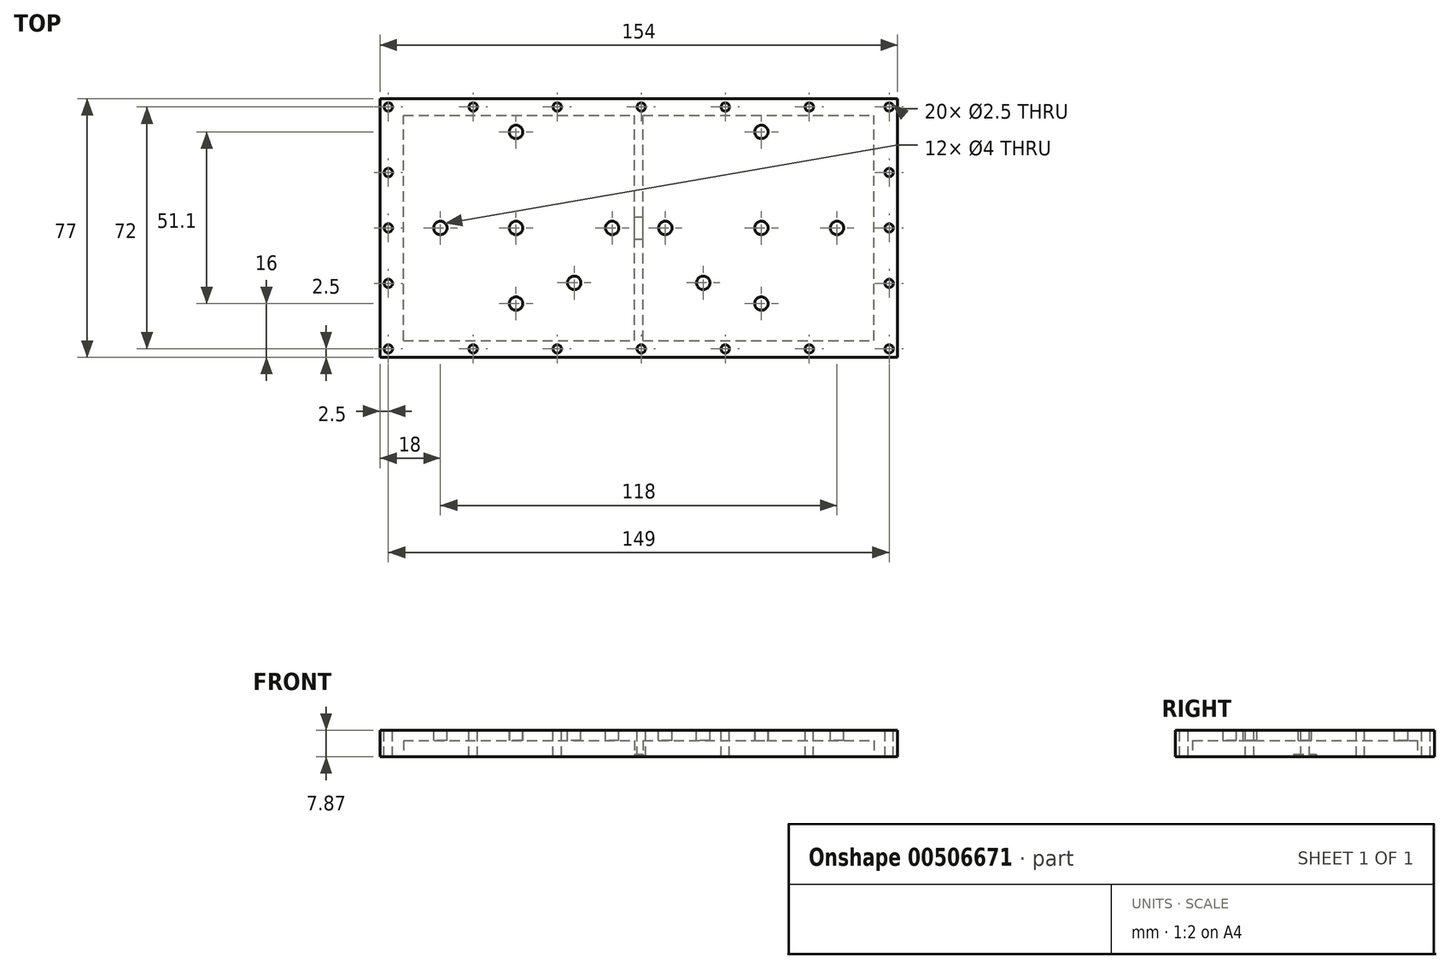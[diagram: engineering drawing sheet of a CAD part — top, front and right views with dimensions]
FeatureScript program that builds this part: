
annotation { "Feature Type Name" : "Feature", "Feature Type Description" : "" }
export const myFeature = defineFeature(function(context is Context, id is Id, definition is map)
    precondition{}
    {
        {
            var Q0;
            Q0=qCreatedBy(makeId("Top.planeOp"),FACE);
            var sketch = newSketch(context, id + "F0", { "sketchPlane" : qUnion([Q0])});
            skLineSegment(sketch, "E0.bottom", {"start": v(0, 0) * mm, "end": v(154, 0) * mm});
            skLineSegment(sketch, "E0.top", {"start": v(0, 77) * mm, "end": v(154, 77) * mm});
            skLineSegment(sketch, "E0.left", {"start": v(0, 0) * mm, "end": v(0, 77) * mm});
            skLineSegment(sketch, "E0.right", {"start": v(154, 0) * mm, "end": v(154, 77) * mm});
            skSolve(sketch);
        }
        {
            var Q0;
            Q0=qSketchRegion(id+"F0",true);
            extrude(context, id + "F1", {"entities" : qUnion([Q0]), "depth" : 7.87 * mm});
        }
        {
            var Q0;
            Q0=qCreatedBy(makeId("Top.planeOp"),FACE);
            var sketch = newSketch(context, id + "F2", { "sketchPlane" : qUnion([Q0])});
            skLineSegment(sketch, "E1.bottom", {"start": v(7, 5) * mm, "end": v(147, 5) * mm});
            skLineSegment(sketch, "E1.top", {"start": v(7, 72) * mm, "end": v(147, 72) * mm});
            skLineSegment(sketch, "E1.left", {"start": v(7, 5) * mm, "end": v(7, 72) * mm});
            skLineSegment(sketch, "E1.right", {"start": v(147, 5) * mm, "end": v(147, 72) * mm});
            skSolve(sketch);
        }
        {
            var Q0;
            Q0=qSketchRegion(id+"F2",true);
            extrude(context, id + "F3", {"entities" : qUnion([Q0]), "operationType" : NewBodyOperationType.REMOVE, "depth" : 4.87 * mm});
        }
        {
            var Q0;
            Q0=makeQuery(id+"F1.opExtrude","CAP_FACE",FACE,{"disambiguationData":[OSD([sQuery(id+"F0.wireOp",EDGE,"E0.bottom"),sQuery(id+"F0.wireOp",EDGE,"E0.top"),sQuery(id+"F0.wireOp",EDGE,"E0.left"),sQuery(id+"F0.wireOp",EDGE,"E0.right")])],"isStart":false});
            var sketch = newSketch(context, id + "F4", { "sketchPlane" : qUnion([Q0])});
            skCircle(sketch, "E2", {"center": v(2.5, 2.5) * mm, "radius": 1.25 * mm});
            skSolve(sketch);
        }
        {
            var Q0;
            Q0=qSketchRegion(id+"F4",true);
            extrude(context, id + "F5", {"entities" : qUnion([Q0]), "operationType" : NewBodyOperationType.REMOVE, "oppositeDirection" : true, "depth" : 7.87 * mm});
        }
        {
            var Q0;
            Q0=makeQuery(id+"F1.opExtrude","CAP_FACE",FACE,{"disambiguationData":[OSD([sQuery(id+"F0.wireOp",EDGE,"E0.bottom"),sQuery(id+"F0.wireOp",EDGE,"E0.top"),sQuery(id+"F0.wireOp",EDGE,"E0.left"),sQuery(id+"F0.wireOp",EDGE,"E0.right")])],"isStart":false});
            var sketch = newSketch(context, id + "F6", { "sketchPlane" : qUnion([Q0])});
            skCircle(sketch, "E3", {"center": v(27.75, 2.5) * mm, "radius": 1.25 * mm});
            skSolve(sketch);
        }
        {
            var Q0;
            Q0=qSketchRegion(id+"F6",true);
            extrude(context, id + "F7", {"entities" : qUnion([Q0]), "operationType" : NewBodyOperationType.REMOVE, "oppositeDirection" : true, "depth" : 7.87 * mm});
        }
        {
            var Q0;
            Q0=makeQuery(id+"F1.opExtrude","CAP_FACE",FACE,{"disambiguationData":[OSD([sQuery(id+"F0.wireOp",EDGE,"E0.bottom"),sQuery(id+"F0.wireOp",EDGE,"E0.top"),sQuery(id+"F0.wireOp",EDGE,"E0.left"),sQuery(id+"F0.wireOp",EDGE,"E0.right")])],"isStart":false});
            var sketch = newSketch(context, id + "F8", { "sketchPlane" : qUnion([Q0])});
            skCircle(sketch, "E4", {"center": v(52.75, 2.5) * mm, "radius": 1.25 * mm});
            skSolve(sketch);
        }
        {
            var Q0;
            Q0=qSketchRegion(id+"F8",true);
            extrude(context, id + "F9", {"entities" : qUnion([Q0]), "operationType" : NewBodyOperationType.REMOVE, "oppositeDirection" : true, "depth" : 7.87 * mm});
        }
        {
            var Q0;
            Q0=makeQuery(id+"F1.opExtrude","CAP_FACE",FACE,{"disambiguationData":[OSD([sQuery(id+"F0.wireOp",EDGE,"E0.bottom"),sQuery(id+"F0.wireOp",EDGE,"E0.top"),sQuery(id+"F0.wireOp",EDGE,"E0.left"),sQuery(id+"F0.wireOp",EDGE,"E0.right")])],"isStart":false});
            var sketch = newSketch(context, id + "F10", { "sketchPlane" : qUnion([Q0])});
            skCircle(sketch, "E5", {"center": v(77.75, 2.5) * mm, "radius": 1.25 * mm});
            skSolve(sketch);
        }
        {
            var Q0;
            Q0=qSketchRegion(id+"F10",true);
            extrude(context, id + "F11", {"entities" : qUnion([Q0]), "operationType" : NewBodyOperationType.REMOVE, "oppositeDirection" : true, "depth" : 7.87 * mm});
        }
        {
            var Q0;
            Q0=makeQuery(id+"F1.opExtrude","CAP_FACE",FACE,{"disambiguationData":[OSD([sQuery(id+"F0.wireOp",EDGE,"E0.bottom"),sQuery(id+"F0.wireOp",EDGE,"E0.top"),sQuery(id+"F0.wireOp",EDGE,"E0.left"),sQuery(id+"F0.wireOp",EDGE,"E0.right")])],"isStart":false});
            var sketch = newSketch(context, id + "F12", { "sketchPlane" : qUnion([Q0])});
            skCircle(sketch, "E6", {"center": v(102.75, 2.5) * mm, "radius": 1.25 * mm});
            skSolve(sketch);
        }
        {
            var Q0;
            Q0=qSketchRegion(id+"F12",true);
            extrude(context, id + "F13", {"entities" : qUnion([Q0]), "operationType" : NewBodyOperationType.REMOVE, "oppositeDirection" : true, "depth" : 7.87 * mm});
        }
        {
            var Q0;
            Q0=makeQuery(id+"F1.opExtrude","CAP_FACE",FACE,{"disambiguationData":[OSD([sQuery(id+"F0.wireOp",EDGE,"E0.bottom"),sQuery(id+"F0.wireOp",EDGE,"E0.top"),sQuery(id+"F0.wireOp",EDGE,"E0.left"),sQuery(id+"F0.wireOp",EDGE,"E0.right")])],"isStart":false});
            var sketch = newSketch(context, id + "F14", { "sketchPlane" : qUnion([Q0])});
            skCircle(sketch, "E7", {"center": v(127.75, 2.5) * mm, "radius": 1.25 * mm});
            skSolve(sketch);
        }
        {
            var Q0;
            Q0=qSketchRegion(id+"F14",true);
            extrude(context, id + "F15", {"entities" : qUnion([Q0]), "operationType" : NewBodyOperationType.REMOVE, "oppositeDirection" : true, "depth" : 7.87 * mm});
        }
        {
            var Q0;
            Q0=makeQuery(id+"F1.opExtrude","CAP_FACE",FACE,{"disambiguationData":[OSD([sQuery(id+"F0.wireOp",EDGE,"E0.bottom"),sQuery(id+"F0.wireOp",EDGE,"E0.top"),sQuery(id+"F0.wireOp",EDGE,"E0.left"),sQuery(id+"F0.wireOp",EDGE,"E0.right")])],"isStart":false});
            var sketch = newSketch(context, id + "F16", { "sketchPlane" : qUnion([Q0])});
            skCircle(sketch, "E8", {"center": v(151.5, 2.5) * mm, "radius": 1.25 * mm});
            skSolve(sketch);
        }
        {
            var Q0;
            Q0=qSketchRegion(id+"F16",true);
            extrude(context, id + "F17", {"entities" : qUnion([Q0]), "operationType" : NewBodyOperationType.REMOVE, "oppositeDirection" : true, "depth" : 7.87 * mm});
        }
        {
            var Q0;
            Q0=makeQuery(id+"F1.opExtrude","CAP_FACE",FACE,{"disambiguationData":[OSD([sQuery(id+"F0.wireOp",EDGE,"E0.bottom"),sQuery(id+"F0.wireOp",EDGE,"E0.top"),sQuery(id+"F0.wireOp",EDGE,"E0.left"),sQuery(id+"F0.wireOp",EDGE,"E0.right")])],"isStart":false});
            var sketch = newSketch(context, id + "F18", { "sketchPlane" : qUnion([Q0])});
            skCircle(sketch, "E9", {"center": v(2.5, 22) * mm, "radius": 1.25 * mm});
            skSolve(sketch);
        }
        {
            var Q0;
            Q0=qSketchRegion(id+"F18",true);
            extrude(context, id + "F19", {"entities" : qUnion([Q0]), "operationType" : NewBodyOperationType.REMOVE, "oppositeDirection" : true, "depth" : 7.87 * mm});
        }
        {
            var Q0;
            Q0=makeQuery(id+"F1.opExtrude","CAP_FACE",FACE,{"disambiguationData":[OSD([sQuery(id+"F0.wireOp",EDGE,"E0.bottom"),sQuery(id+"F0.wireOp",EDGE,"E0.top"),sQuery(id+"F0.wireOp",EDGE,"E0.left"),sQuery(id+"F0.wireOp",EDGE,"E0.right")])],"isStart":false});
            var sketch = newSketch(context, id + "F20", { "sketchPlane" : qUnion([Q0])});
            skCircle(sketch, "E10", {"center": v(151.5, 22) * mm, "radius": 1.25 * mm});
            skSolve(sketch);
        }
        {
            var Q0;
            Q0=qSketchRegion(id+"F20",true);
            extrude(context, id + "F21", {"entities" : qUnion([Q0]), "operationType" : NewBodyOperationType.REMOVE, "oppositeDirection" : true, "depth" : 7.87 * mm});
        }
        {
            var Q0;
            Q0=makeQuery(id+"F1.opExtrude","CAP_FACE",FACE,{"disambiguationData":[OSD([sQuery(id+"F0.wireOp",EDGE,"E0.bottom"),sQuery(id+"F0.wireOp",EDGE,"E0.top"),sQuery(id+"F0.wireOp",EDGE,"E0.left"),sQuery(id+"F0.wireOp",EDGE,"E0.right")])],"isStart":false});
            var sketch = newSketch(context, id + "F22", { "sketchPlane" : qUnion([Q0])});
            skCircle(sketch, "E11", {"center": v(151.5, 38.5) * mm, "radius": 1.25 * mm});
            skSolve(sketch);
        }
        {
            var Q0;
            Q0=qSketchRegion(id+"F22",true);
            extrude(context, id + "F23", {"entities" : qUnion([Q0]), "operationType" : NewBodyOperationType.REMOVE, "oppositeDirection" : true, "depth" : 7.87 * mm});
        }
        {
            var Q0;
            Q0=makeQuery(id+"F1.opExtrude","CAP_FACE",FACE,{"disambiguationData":[OSD([sQuery(id+"F0.wireOp",EDGE,"E0.bottom"),sQuery(id+"F0.wireOp",EDGE,"E0.top"),sQuery(id+"F0.wireOp",EDGE,"E0.left"),sQuery(id+"F0.wireOp",EDGE,"E0.right")])],"isStart":false});
            var sketch = newSketch(context, id + "F24", { "sketchPlane" : qUnion([Q0])});
            skCircle(sketch, "E12", {"center": v(2.5, 38.5) * mm, "radius": 1.25 * mm});
            skSolve(sketch);
        }
        {
            var Q0;
            Q0=qSketchRegion(id+"F24",true);
            extrude(context, id + "F25", {"entities" : qUnion([Q0]), "operationType" : NewBodyOperationType.REMOVE, "oppositeDirection" : true, "depth" : 7.87 * mm});
        }
        {
            var Q0;
            Q0=makeQuery(id+"F1.opExtrude","CAP_FACE",FACE,{"disambiguationData":[OSD([sQuery(id+"F0.wireOp",EDGE,"E0.bottom"),sQuery(id+"F0.wireOp",EDGE,"E0.top"),sQuery(id+"F0.wireOp",EDGE,"E0.left"),sQuery(id+"F0.wireOp",EDGE,"E0.right")])],"isStart":false});
            var sketch = newSketch(context, id + "F26", { "sketchPlane" : qUnion([Q0])});
            skCircle(sketch, "E13", {"center": v(2.5, 55) * mm, "radius": 1.25 * mm});
            skSolve(sketch);
        }
        {
            var Q0;
            Q0=qSketchRegion(id+"F26",true);
            extrude(context, id + "F27", {"entities" : qUnion([Q0]), "operationType" : NewBodyOperationType.REMOVE, "oppositeDirection" : true, "depth" : 7.87 * mm});
        }
        {
            var Q0;
            Q0=makeQuery(id+"F1.opExtrude","CAP_FACE",FACE,{"disambiguationData":[OSD([sQuery(id+"F0.wireOp",EDGE,"E0.bottom"),sQuery(id+"F0.wireOp",EDGE,"E0.top"),sQuery(id+"F0.wireOp",EDGE,"E0.left"),sQuery(id+"F0.wireOp",EDGE,"E0.right")])],"isStart":false});
            var sketch = newSketch(context, id + "F28", { "sketchPlane" : qUnion([Q0])});
            skCircle(sketch, "E14", {"center": v(151.5, 55) * mm, "radius": 1.25 * mm});
            skSolve(sketch);
        }
        {
            var Q0;
            Q0=qSketchRegion(id+"F28",true);
            extrude(context, id + "F29", {"entities" : qUnion([Q0]), "operationType" : NewBodyOperationType.REMOVE, "oppositeDirection" : true, "depth" : 7.87 * mm});
        }
        {
            var Q0;
            Q0=makeQuery(id+"F1.opExtrude","CAP_FACE",FACE,{"disambiguationData":[OSD([sQuery(id+"F0.wireOp",EDGE,"E0.bottom"),sQuery(id+"F0.wireOp",EDGE,"E0.top"),sQuery(id+"F0.wireOp",EDGE,"E0.left"),sQuery(id+"F0.wireOp",EDGE,"E0.right")])],"isStart":false});
            var sketch = newSketch(context, id + "F30", { "sketchPlane" : qUnion([Q0])});
            skCircle(sketch, "E15", {"center": v(2.5, 74.5) * mm, "radius": 1.25 * mm});
            skSolve(sketch);
        }
        {
            var Q0;
            Q0=qSketchRegion(id+"F30",true);
            extrude(context, id + "F31", {"entities" : qUnion([Q0]), "operationType" : NewBodyOperationType.REMOVE, "oppositeDirection" : true, "depth" : 7.87 * mm});
        }
        {
            var Q0;
            Q0=makeQuery(id+"F1.opExtrude","CAP_FACE",FACE,{"disambiguationData":[OSD([sQuery(id+"F0.wireOp",EDGE,"E0.bottom"),sQuery(id+"F0.wireOp",EDGE,"E0.top"),sQuery(id+"F0.wireOp",EDGE,"E0.left"),sQuery(id+"F0.wireOp",EDGE,"E0.right")])],"isStart":false});
            var sketch = newSketch(context, id + "F32", { "sketchPlane" : qUnion([Q0])});
            skCircle(sketch, "E16", {"center": v(151.5, 74.5) * mm, "radius": 1.25 * mm});
            skSolve(sketch);
        }
        {
            var Q0;
            Q0=qSketchRegion(id+"F32",true);
            extrude(context, id + "F33", {"entities" : qUnion([Q0]), "operationType" : NewBodyOperationType.REMOVE, "oppositeDirection" : true, "depth" : 7.87 * mm});
        }
        {
            var Q0;
            Q0=makeQuery(id+"F1.opExtrude","CAP_FACE",FACE,{"disambiguationData":[OSD([sQuery(id+"F0.wireOp",EDGE,"E0.bottom"),sQuery(id+"F0.wireOp",EDGE,"E0.top"),sQuery(id+"F0.wireOp",EDGE,"E0.left"),sQuery(id+"F0.wireOp",EDGE,"E0.right")])],"isStart":false});
            var sketch = newSketch(context, id + "F34", { "sketchPlane" : qUnion([Q0])});
            skCircle(sketch, "E17", {"center": v(27.75, 74.5) * mm, "radius": 1.25 * mm});
            skSolve(sketch);
        }
        {
            var Q0;
            Q0=qSketchRegion(id+"F34",true);
            extrude(context, id + "F35", {"entities" : qUnion([Q0]), "operationType" : NewBodyOperationType.REMOVE, "oppositeDirection" : true, "depth" : 7.87 * mm});
        }
        {
            var Q0;
            Q0=makeQuery(id+"F1.opExtrude","CAP_FACE",FACE,{"disambiguationData":[OSD([sQuery(id+"F0.wireOp",EDGE,"E0.bottom"),sQuery(id+"F0.wireOp",EDGE,"E0.top"),sQuery(id+"F0.wireOp",EDGE,"E0.left"),sQuery(id+"F0.wireOp",EDGE,"E0.right")])],"isStart":false});
            var sketch = newSketch(context, id + "F36", { "sketchPlane" : qUnion([Q0])});
            skCircle(sketch, "E18", {"center": v(127.75, 74.5) * mm, "radius": 1.25 * mm});
            skSolve(sketch);
        }
        {
            var Q0;
            Q0=qSketchRegion(id+"F36",true);
            extrude(context, id + "F37", {"entities" : qUnion([Q0]), "operationType" : NewBodyOperationType.REMOVE, "oppositeDirection" : true, "depth" : 7.87 * mm});
        }
        {
            var Q0;
            Q0=makeQuery(id+"F1.opExtrude","CAP_FACE",FACE,{"disambiguationData":[OSD([sQuery(id+"F0.wireOp",EDGE,"E0.bottom"),sQuery(id+"F0.wireOp",EDGE,"E0.top"),sQuery(id+"F0.wireOp",EDGE,"E0.left"),sQuery(id+"F0.wireOp",EDGE,"E0.right")])],"isStart":false});
            var sketch = newSketch(context, id + "F38", { "sketchPlane" : qUnion([Q0])});
            skCircle(sketch, "E19", {"center": v(102.75, 74.5) * mm, "radius": 1.25 * mm});
            skSolve(sketch);
        }
        {
            var Q0;
            Q0=qSketchRegion(id+"F38",true);
            extrude(context, id + "F39", {"entities" : qUnion([Q0]), "operationType" : NewBodyOperationType.REMOVE, "oppositeDirection" : true, "depth" : 7.87 * mm});
        }
        {
            var Q0;
            Q0=makeQuery(id+"F1.opExtrude","CAP_FACE",FACE,{"disambiguationData":[OSD([sQuery(id+"F0.wireOp",EDGE,"E0.bottom"),sQuery(id+"F0.wireOp",EDGE,"E0.top"),sQuery(id+"F0.wireOp",EDGE,"E0.left"),sQuery(id+"F0.wireOp",EDGE,"E0.right")])],"isStart":false});
            var sketch = newSketch(context, id + "F40", { "sketchPlane" : qUnion([Q0])});
            skCircle(sketch, "E20", {"center": v(52.75, 74.5) * mm, "radius": 1.25 * mm});
            skSolve(sketch);
        }
        {
            var Q0;
            Q0=qSketchRegion(id+"F40",true);
            extrude(context, id + "F41", {"entities" : qUnion([Q0]), "operationType" : NewBodyOperationType.REMOVE, "oppositeDirection" : true, "depth" : 7.87 * mm});
        }
        {
            var Q0;
            Q0=makeQuery(id+"F1.opExtrude","CAP_FACE",FACE,{"disambiguationData":[OSD([sQuery(id+"F0.wireOp",EDGE,"E0.bottom"),sQuery(id+"F0.wireOp",EDGE,"E0.top"),sQuery(id+"F0.wireOp",EDGE,"E0.left"),sQuery(id+"F0.wireOp",EDGE,"E0.right")])],"isStart":false});
            var sketch = newSketch(context, id + "F42", { "sketchPlane" : qUnion([Q0])});
            skCircle(sketch, "E21", {"center": v(77.75, 74.5) * mm, "radius": 1.25 * mm});
            skSolve(sketch);
        }
        {
            var Q0;
            Q0=qSketchRegion(id+"F42",true);
            extrude(context, id + "F43", {"entities" : qUnion([Q0]), "operationType" : NewBodyOperationType.REMOVE, "oppositeDirection" : true, "depth" : 7.87 * mm});
        }
        {
            var Q0;
            Q0=makeQuery(id+"F1.opExtrude","CAP_FACE",FACE,{"disambiguationData":[OSD([sQuery(id+"F0.wireOp",EDGE,"E0.bottom"),sQuery(id+"F0.wireOp",EDGE,"E0.top"),sQuery(id+"F0.wireOp",EDGE,"E0.left"),sQuery(id+"F0.wireOp",EDGE,"E0.right")])],"isStart":false});
            var sketch = newSketch(context, id + "F44", { "sketchPlane" : qUnion([Q0])});
            skCircle(sketch, "E22", {"center": v(40.5, 67.1) * mm, "radius": 2 * mm});
            skSolve(sketch);
        }
        {
            var Q0;
            Q0=qSketchRegion(id+"F44",true);
            extrude(context, id + "F45", {"entities" : qUnion([Q0]), "operationType" : NewBodyOperationType.REMOVE, "oppositeDirection" : true, "depth" : 3 * mm});
        }
        {
            var Q0;
            Q0=makeQuery(id+"F1.opExtrude","CAP_FACE",FACE,{"disambiguationData":[OSD([sQuery(id+"F0.wireOp",EDGE,"E0.bottom"),sQuery(id+"F0.wireOp",EDGE,"E0.top"),sQuery(id+"F0.wireOp",EDGE,"E0.left"),sQuery(id+"F0.wireOp",EDGE,"E0.right")])],"isStart":false});
            var sketch = newSketch(context, id + "F46", { "sketchPlane" : qUnion([Q0])});
            skCircle(sketch, "E23", {"center": v(18, 38.5) * mm, "radius": 2 * mm});
            skSolve(sketch);
        }
        {
            var Q0;
            Q0=qSketchRegion(id+"F46",true);
            extrude(context, id + "F47", {"entities" : qUnion([Q0]), "operationType" : NewBodyOperationType.REMOVE, "oppositeDirection" : true, "depth" : 3 * mm});
        }
        {
            var Q0;
            Q0=makeQuery(id+"F1.opExtrude","CAP_FACE",FACE,{"disambiguationData":[OSD([sQuery(id+"F0.wireOp",EDGE,"E0.bottom"),sQuery(id+"F0.wireOp",EDGE,"E0.top"),sQuery(id+"F0.wireOp",EDGE,"E0.left"),sQuery(id+"F0.wireOp",EDGE,"E0.right")])],"isStart":false});
            var sketch = newSketch(context, id + "F48", { "sketchPlane" : qUnion([Q0])});
            skCircle(sketch, "E24", {"center": v(69.1, 38.5) * mm, "radius": 2 * mm});
            skSolve(sketch);
        }
        {
            var Q0;
            Q0=qSketchRegion(id+"F48",true);
            extrude(context, id + "F49", {"entities" : qUnion([Q0]), "operationType" : NewBodyOperationType.REMOVE, "oppositeDirection" : true, "depth" : 3 * mm});
        }
        {
            var Q0;
            Q0=makeQuery(id+"F1.opExtrude","CAP_FACE",FACE,{"disambiguationData":[OSD([sQuery(id+"F0.wireOp",EDGE,"E0.bottom"),sQuery(id+"F0.wireOp",EDGE,"E0.top"),sQuery(id+"F0.wireOp",EDGE,"E0.left"),sQuery(id+"F0.wireOp",EDGE,"E0.right")])],"isStart":false});
            var sketch = newSketch(context, id + "F50", { "sketchPlane" : qUnion([Q0])});
            skCircle(sketch, "E25", {"center": v(113.5, 67.1) * mm, "radius": 2 * mm});
            skSolve(sketch);
        }
        {
            var Q0;
            Q0=qSketchRegion(id+"F50",true);
            extrude(context, id + "F51", {"entities" : qUnion([Q0]), "operationType" : NewBodyOperationType.REMOVE, "oppositeDirection" : true, "depth" : 3 * mm});
        }
        {
            var Q0;
            Q0=makeQuery(id+"F1.opExtrude","CAP_FACE",FACE,{"disambiguationData":[OSD([sQuery(id+"F0.wireOp",EDGE,"E0.bottom"),sQuery(id+"F0.wireOp",EDGE,"E0.top"),sQuery(id+"F0.wireOp",EDGE,"E0.left"),sQuery(id+"F0.wireOp",EDGE,"E0.right")])],"isStart":false});
            var sketch = newSketch(context, id + "F52", { "sketchPlane" : qUnion([Q0])});
            skCircle(sketch, "E26", {"center": v(84.9, 38.5) * mm, "radius": 2 * mm});
            skSolve(sketch);
        }
        {
            var Q0;
            Q0=qSketchRegion(id+"F52",true);
            extrude(context, id + "F53", {"entities" : qUnion([Q0]), "operationType" : NewBodyOperationType.REMOVE, "oppositeDirection" : true, "depth" : 3 * mm});
        }
        {
            var Q0;
            Q0=makeQuery(id+"F1.opExtrude","CAP_FACE",FACE,{"disambiguationData":[OSD([sQuery(id+"F0.wireOp",EDGE,"E0.bottom"),sQuery(id+"F0.wireOp",EDGE,"E0.top"),sQuery(id+"F0.wireOp",EDGE,"E0.left"),sQuery(id+"F0.wireOp",EDGE,"E0.right")])],"isStart":false});
            var sketch = newSketch(context, id + "F54", { "sketchPlane" : qUnion([Q0])});
            skCircle(sketch, "E27", {"center": v(136, 38.5) * mm, "radius": 2 * mm});
            skSolve(sketch);
        }
        {
            var Q0;
            Q0=qSketchRegion(id+"F54",true);
            extrude(context, id + "F55", {"entities" : qUnion([Q0]), "operationType" : NewBodyOperationType.REMOVE, "oppositeDirection" : true, "depth" : 3 * mm});
        }
        {
            var Q0;
            Q0=makeQuery(id+"F1.opExtrude","CAP_FACE",FACE,{"disambiguationData":[OSD([sQuery(id+"F0.wireOp",EDGE,"E0.bottom"),sQuery(id+"F0.wireOp",EDGE,"E0.top"),sQuery(id+"F0.wireOp",EDGE,"E0.left"),sQuery(id+"F0.wireOp",EDGE,"E0.right")])],"isStart":false});
            var sketch = newSketch(context, id + "F56", { "sketchPlane" : qUnion([Q0])});
            skCircle(sketch, "E28", {"center": v(57.8, 22.17) * mm, "radius": 2 * mm});
            skSolve(sketch);
        }
        {
            var Q0;
            Q0=qSketchRegion(id+"F56",true);
            extrude(context, id + "F57", {"entities" : qUnion([Q0]), "operationType" : NewBodyOperationType.REMOVE, "oppositeDirection" : true, "depth" : 3 * mm});
        }
        {
            var Q0;
            Q0=makeQuery(id+"F1.opExtrude","CAP_FACE",FACE,{"disambiguationData":[OSD([sQuery(id+"F0.wireOp",EDGE,"E0.bottom"),sQuery(id+"F0.wireOp",EDGE,"E0.top"),sQuery(id+"F0.wireOp",EDGE,"E0.left"),sQuery(id+"F0.wireOp",EDGE,"E0.right")])],"isStart":false});
            var sketch = newSketch(context, id + "F58", { "sketchPlane" : qUnion([Q0])});
            skCircle(sketch, "E29", {"center": v(96.2, 22.17) * mm, "radius": 2 * mm});
            skSolve(sketch);
        }
        {
            var Q0;
            Q0=qSketchRegion(id+"F58",true);
            extrude(context, id + "F59", {"entities" : qUnion([Q0]), "operationType" : NewBodyOperationType.REMOVE, "oppositeDirection" : true, "depth" : 3 * mm});
        }
        {
            var Q0;
            Q0=makeQuery(id+"F1.opExtrude","CAP_FACE",FACE,{"disambiguationData":[OSD([sQuery(id+"F0.wireOp",EDGE,"E0.bottom"),sQuery(id+"F0.wireOp",EDGE,"E0.top"),sQuery(id+"F0.wireOp",EDGE,"E0.left"),sQuery(id+"F0.wireOp",EDGE,"E0.right")])],"isStart":true});
            var sketch = newSketch(context, id + "F60", { "sketchPlane" : qUnion([Q0])});
            skLineSegment(sketch, "E30.bottom", {"start": v(75.75, -35.15) * mm, "end": v(78.25, -35.15) * mm});
            skLineSegment(sketch, "E30.top", {"start": v(75.75, -41.85) * mm, "end": v(78.25, -41.85) * mm});
            skLineSegment(sketch, "E30.left", {"start": v(75.75, -35.15) * mm, "end": v(75.75, -41.85) * mm});
            skLineSegment(sketch, "E30.right", {"start": v(78.25, -35.15) * mm, "end": v(78.25, -41.85) * mm});
            skSolve(sketch);
        }
        {
            var Q0;
            {var subQ0=sQuery(id+"F2.wireOp",EDGE,"E1.top");var subQ1=sQuery(id+"F2.wireOp",EDGE,"E1.bottom");var subQ2=sQuery(id+"F2.wireOp",EDGE,"E1.left");Q0=makeQuery(id+"FZ5JwFvxZTi6GKV_1.boolean.opBoolean","SPLIT",FACE,{"disambiguationData":[TD([makeQuery(id+"F3.boolean.opBoolean","COPY",FACE,{"derivedFrom":makeQuery(id+"F3.opExtrude","SWEPT_FACE",FACE,{"disambiguationData":[OSD([subQ2])]})})])],"derivedFrom":makeQuery(id+"F3.boolean.opBoolean","COPY",FACE,{"derivedFrom":makeQuery(id+"F3.opExtrude","CAP_FACE",FACE,{"disambiguationData":[OSD([subQ1,subQ0,subQ2,sQuery(id+"F2.wireOp",EDGE,"E1.right")])],"isStart":false})})});}
            var sketch = newSketch(context, id + "F61", { "sketchPlane" : qUnion([Q0])});
            skCircle(sketch, "E31", {"center": v(40.5, -16) * mm, "radius": 2 * mm});
            skSolve(sketch);
        }
        {
            var Q0;
            Q0=qSketchRegion(id+"F61",true);
            extrude(context, id + "F62", {"entities" : qUnion([Q0]), "operationType" : NewBodyOperationType.REMOVE, "oppositeDirection" : true, "depth" : 3 * mm});
        }
        {
            var Q0;
            {var subQ0=sQuery(id+"F2.wireOp",EDGE,"E1.left");var subQ1=sQuery(id+"F2.wireOp",EDGE,"E1.top");var subQ2=sQuery(id+"F2.wireOp",EDGE,"E1.bottom");Q0=makeQuery(id+"FZ5JwFvxZTi6GKV_1.boolean.opBoolean","SPLIT",FACE,{"disambiguationData":[TD([makeQuery(id+"F3.boolean.opBoolean","COPY",FACE,{"derivedFrom":makeQuery(id+"F3.opExtrude","SWEPT_FACE",FACE,{"disambiguationData":[OSD([subQ0])]})})])],"derivedFrom":makeQuery(id+"F3.boolean.opBoolean","COPY",FACE,{"derivedFrom":makeQuery(id+"F3.opExtrude","CAP_FACE",FACE,{"disambiguationData":[OSD([subQ2,subQ1,subQ0,sQuery(id+"F2.wireOp",EDGE,"E1.right")])],"isStart":false})})});}
            var sketch = newSketch(context, id + "F63", { "sketchPlane" : qUnion([Q0])});
            skCircle(sketch, "E32", {"center": v(40.5, -38.5) * mm, "radius": 2 * mm});
            skSolve(sketch);
        }
        {
            var Q0;
            {var subQ0=sQuery(id+"F2.wireOp",EDGE,"E1.right");var subQ1=sQuery(id+"F2.wireOp",EDGE,"E1.top");var subQ2=sQuery(id+"F2.wireOp",EDGE,"E1.bottom");Q0=makeQuery(id+"FZ5JwFvxZTi6GKV_1.boolean.opBoolean","SPLIT",FACE,{"disambiguationData":[TD([makeQuery(id+"F3.boolean.opBoolean","COPY",FACE,{"derivedFrom":makeQuery(id+"F3.opExtrude","SWEPT_FACE",FACE,{"disambiguationData":[OSD([subQ0])]})})])],"derivedFrom":makeQuery(id+"F3.boolean.opBoolean","COPY",FACE,{"derivedFrom":makeQuery(id+"F3.opExtrude","CAP_FACE",FACE,{"disambiguationData":[OSD([subQ2,subQ1,sQuery(id+"F2.wireOp",EDGE,"E1.left"),subQ0])],"isStart":false})})});}
            var sketch = newSketch(context, id + "F64", { "sketchPlane" : qUnion([Q0])});
            skCircle(sketch, "E33", {"center": v(113.5, -38.5) * mm, "radius": 2 * mm});
            skSolve(sketch);
        }
        {
            var Q0;
            Q0=qSketchRegion(id+"F64",true);
            extrude(context, id + "F65", {"entities" : qUnion([Q0]), "operationType" : NewBodyOperationType.REMOVE, "oppositeDirection" : true, "depth" : 3 * mm});
        }
        {
            var Q0;
            {var subQ0=sQuery(id+"F2.wireOp",EDGE,"E1.right");var subQ1=sQuery(id+"F2.wireOp",EDGE,"E1.top");var subQ2=sQuery(id+"F2.wireOp",EDGE,"E1.bottom");Q0=makeQuery(id+"FZ5JwFvxZTi6GKV_1.boolean.opBoolean","SPLIT",FACE,{"disambiguationData":[TD([makeQuery(id+"F3.boolean.opBoolean","COPY",FACE,{"derivedFrom":makeQuery(id+"F3.opExtrude","SWEPT_FACE",FACE,{"disambiguationData":[OSD([subQ0])]})})])],"derivedFrom":makeQuery(id+"F3.boolean.opBoolean","COPY",FACE,{"derivedFrom":makeQuery(id+"F3.opExtrude","CAP_FACE",FACE,{"disambiguationData":[OSD([subQ2,subQ1,sQuery(id+"F2.wireOp",EDGE,"E1.left"),subQ0])],"isStart":false})})});}
            var sketch = newSketch(context, id + "F66", { "sketchPlane" : qUnion([Q0])});
            skCircle(sketch, "E34", {"center": v(113.5, -16) * mm, "radius": 2 * mm});
            skSolve(sketch);
        }
        {
            var Q0;
            Q0=qSketchRegion(id+"F66",true);
            extrude(context, id + "F67", {"entities" : qUnion([Q0]), "operationType" : NewBodyOperationType.REMOVE, "oppositeDirection" : true, "depth" : 3 * mm});
        }
        {
            var Q0;
            Q0=qSketchRegion(id+"F63",true);
            extrude(context, id + "F68", {"entities" : qUnion([Q0]), "operationType" : NewBodyOperationType.REMOVE, "oppositeDirection" : true, "depth" : 3 * mm});
        }
        {
            var Q0;
            Q0=makeQuery(id+"F1.opExtrude","CAP_FACE",FACE,{"disambiguationData":[OSD([sQuery(id+"F0.wireOp",EDGE,"E0.bottom"),sQuery(id+"F0.wireOp",EDGE,"E0.top"),sQuery(id+"F0.wireOp",EDGE,"E0.left"),sQuery(id+"F0.wireOp",EDGE,"E0.right")])],"isStart":true});
            var sketch = newSketch(context, id + "F69", { "sketchPlane" : qUnion([Q0])});
            skLineSegment(sketch, "E35.bottom", {"start": v(75.75, -5) * mm, "end": v(78.25, -5) * mm});
            skLineSegment(sketch, "E35.top", {"start": v(75.75, -72) * mm, "end": v(78.25, -72) * mm});
            skLineSegment(sketch, "E35.left", {"start": v(75.75, -5) * mm, "end": v(75.75, -72) * mm});
            skLineSegment(sketch, "E35.right", {"start": v(78.25, -5) * mm, "end": v(78.25, -72) * mm});
            skSolve(sketch);
        }
        {
            var Q0;
            Q0 = qSketchRegion(id + "F69", true);
            extrude(context, id + "F70", {"entities" : qUnion([Q0]), "operationType" : NewBodyOperationType.ADD, "oppositeDirection" : true, "depth" : 4.87 * mm});
        }
        {
            var Q0;
            Q0 = qSketchRegion(id + "F60", true);
            extrude(context, id + "F71", {"entities" : qUnion([Q0]), "operationType" : NewBodyOperationType.REMOVE, "oppositeDirection" : true, "depth" : 0.72 * mm});
        }
    });
